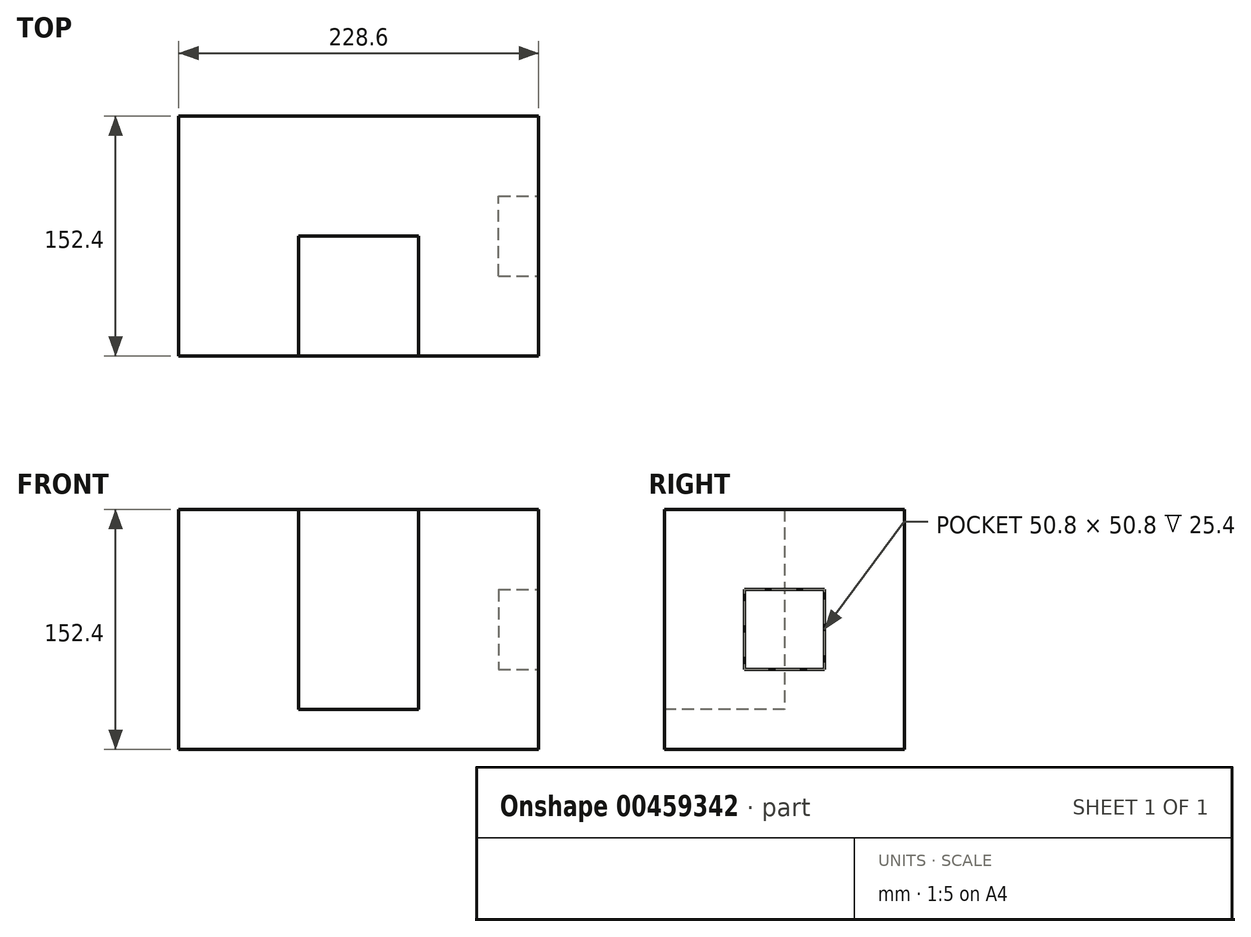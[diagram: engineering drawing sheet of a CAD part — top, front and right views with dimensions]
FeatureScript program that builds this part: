
annotation { "Feature Type Name" : "Feature", "Feature Type Description" : "" }
export const myFeature = defineFeature(function(context is Context, id is Id, definition is map)
    precondition{}
    {
        {
            var Q0;
            Q0=qCreatedBy(makeId("Top.planeOp"),FACE);
            var sketch = newSketch(context, id + "F0", { "sketchPlane" : qUnion([Q0])});
            skLineSegment(sketch, "E0.bottom", {"start": v(-114.3, 76.2) * mm, "end": v(114.3, 76.2) * mm});
            skLineSegment(sketch, "E0.top", {"start": v(-114.3, -76.2) * mm, "end": v(114.3, -76.2) * mm});
            skLineSegment(sketch, "E0.left", {"start": v(-114.3, 76.2) * mm, "end": v(-114.3, -76.2) * mm});
            skLineSegment(sketch, "E0.right", {"start": v(114.3, 76.2) * mm, "end": v(114.3, -76.2) * mm});
            skPoint(sketch, "E0.middle", {"position": v(0, 0) * mm});
            skSolve(sketch);
        }
        {
            var Q0;
            Q0=makeQuery(id+"F0.imprint","IMPRINT",FACE,{"disambiguationData":[TD([[makeQuery(id+"F0.imprint","IMPRINT",EDGE,{"derivedFrom":sQuery(id+"F0.wireOp",EDGE,"E0.bottom")}),-1.0]])]});
            extrude(context, id + "F1", {"entities" : qUnion([Q0]), "endBound" : BoundingType.SYMMETRIC, "depth" : 152.4 * mm});
        }
        {
            var Q0;
            Q0=makeQuery(id+"F1.opExtrude","SWEPT_FACE",FACE,{"disambiguationData":[OSD([sQuery(id+"F0.wireOp",EDGE,"E0.right")])]});
            var sketch = newSketch(context, id + "F2", { "sketchPlane" : qUnion([Q0])});
            skLineSegment(sketch, "E1.bottom", {"start": v(-25.4, 25.4) * mm, "end": v(25.4, 25.4) * mm});
            skLineSegment(sketch, "E1.top", {"start": v(-25.4, -25.4) * mm, "end": v(25.4, -25.4) * mm});
            skLineSegment(sketch, "E1.left", {"start": v(-25.4, 25.4) * mm, "end": v(-25.4, -25.4) * mm});
            skLineSegment(sketch, "E1.right", {"start": v(25.4, 25.4) * mm, "end": v(25.4, -25.4) * mm});
            skPoint(sketch, "E1.middle", {"position": v(0, 0) * mm});
            skSolve(sketch);
        }
        {
            var Q0;
            Q0=makeQuery(id+"F2.imprint","IMPRINT",FACE,{"disambiguationData":[TD([[makeQuery(id+"F2.imprint","IMPRINT",EDGE,{"derivedFrom":sQuery(id+"F2.wireOp",EDGE,"E1.bottom")}),-1.0]])]});
            extrude(context, id + "F3", {"entities" : qUnion([Q0]), "operationType" : NewBodyOperationType.REMOVE, "oppositeDirection" : true, "depth" : 25.4 * mm});
        }
        {
            var Q0;
            Q0=makeQuery(id+"F1.opExtrude","SWEPT_FACE",FACE,{"disambiguationData":[OSD([sQuery(id+"F0.wireOp",EDGE,"E0.top")])]});
            var sketch = newSketch(context, id + "F4", { "sketchPlane" : qUnion([Q0])});
            skLineSegment(sketch, "E2.bottom", {"start": v(-38.1, 76.2) * mm, "end": v(38.1, 76.2) * mm});
            skLineSegment(sketch, "E2.top", {"start": v(-38.1, -50.8) * mm, "end": v(38.1, -50.8) * mm});
            skLineSegment(sketch, "E2.left", {"start": v(-38.1, 76.2) * mm, "end": v(-38.1, -50.8) * mm});
            skLineSegment(sketch, "E2.right", {"start": v(38.1, 76.2) * mm, "end": v(38.1, -50.8) * mm});
            skSolve(sketch);
        }
        {
            var Q0;
            Q0=makeQuery(id+"F4.imprint","IMPRINT",FACE,{"disambiguationData":[TD([[makeQuery(id+"F4.imprint","IMPRINT",EDGE,{"derivedFrom":sQuery(id+"F4.wireOp",EDGE,"E2.bottom")}),-1.0]])]});
            extrude(context, id + "F5", {"entities" : qUnion([Q0]), "operationType" : NewBodyOperationType.REMOVE, "oppositeDirection" : true, "depth" : 76.2 * mm});
        }
    });
